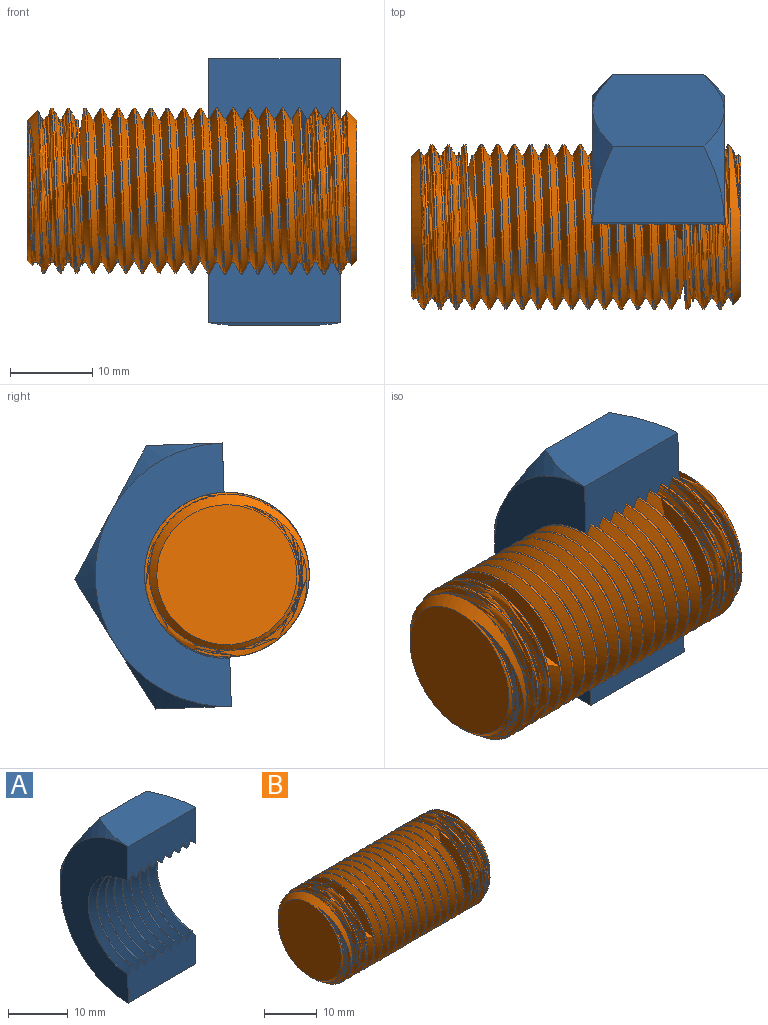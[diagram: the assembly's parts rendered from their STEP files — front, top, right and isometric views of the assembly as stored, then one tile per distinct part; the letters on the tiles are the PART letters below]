
ASSEMBLY  parts=2 mates=1
PART A: 49 faces, bbox 18.7x28.2x37.9 mm
  f0: plane 16x7.23mm, normal (0,-1,0), area 105.3mm2, adj f9,f11,f12,f13,f14,f15,f16,f17
  f1: cone r=18.5mm half-angle=45deg, axis (-1,0,0), area 19.5mm2, adj f2,f4,f47
  f2: plane 16.01x16mm, normal (0,0.87,-0.5), area 264.2mm2, adj f1,f3,f4,f6,f7,f8
  f3: cone r=18.5mm half-angle=45deg, axis (-1,0,0), area 19.5mm2, adj f2,f6,f47
  f4: plane 16.01x16mm, normal (0,0.87,0.5), area 264.2mm2, adj f1,f2,f5,f8,f9,f10
  f5: cone r=18.5mm half-angle=45deg, axis (-1,0,0), area 19.5mm2, adj f4,f9,f47
  f6: plane 16.01x9.24mm, normal (0,0,-1), area 132.1mm2, adj f2,f3,f7,f48
  f7: cone r=18.5mm half-angle=45deg, axis (1,0,0), area 19.5mm2, adj f2,f6,f46
  f8: cone r=18.5mm half-angle=45deg, axis (1,0,0), area 19.5mm2, adj f2,f4,f46
  f9: plane 16.01x9.24mm, normal (0,0,1), area 132.1mm2, adj f0,f4,f5,f10
  f10: cone r=18.5mm half-angle=45deg, axis (1,0,0), area 19.5mm2, adj f4,f9,f46
  f11: cylinder r=8.77mm len=17.53mm, axis (-1,0,0), area 7.2mm2, adj f0,f12,f19,f48
  f12: bspline ~20.54x20.33mm, area 48.1mm2, adj f0,f11,f13,f48
  f13: cylinder r=10.17mm len=20.33mm, axis (-1,0,0), area 3.9mm2, adj f0,f12,f15,f46,f48
  f14: cylinder r=8.77mm len=3.52mm, axis (-1,0,0), area 0.2mm2, adj f0,f15,f46
  f15: bspline ~20.54x20.33mm, area 26.1mm2, adj f0,f13,f14,f46
  f16: cylinder r=8.77mm len=17.53mm, axis (-1,0,0), area 7.2mm2, adj f0,f17,f23,f48
  f17: bspline ~20.54x20.33mm, area 48.1mm2, adj f0,f16,f18,f48
  f18: cylinder r=10.17mm len=20.33mm, axis (-1,0,0), area 4mm2, adj f0,f17,f19,f48
  f19: bspline ~20.54x20.33mm, area 48.1mm2, adj f0,f11,f18,f48
  f20: cylinder r=8.77mm len=17.53mm, axis (-1,0,0), area 7.2mm2, adj f0,f21,f27,f48
  f21: bspline ~20.54x20.33mm, area 48.1mm2, adj f0,f20,f22,f48
  f22: cylinder r=10.17mm len=20.33mm, axis (-1,0,0), area 4mm2, adj f0,f21,f23,f48
  f23: bspline ~20.54x20.33mm, area 48.1mm2, adj f0,f16,f22,f48
  f24: cylinder r=8.77mm len=17.53mm, axis (-1,0,0), area 7.2mm2, adj f0,f25,f31,f48
  f25: bspline ~20.54x20.33mm, area 48.1mm2, adj f0,f24,f26,f48
  f26: cylinder r=10.17mm len=20.33mm, axis (-1,0,0), area 4mm2, adj f0,f25,f27,f48
  f27: bspline ~20.54x20.33mm, area 48.1mm2, adj f0,f20,f26,f48
  f28: cylinder r=8.77mm len=17.53mm, axis (-1,0,0), area 7.2mm2, adj f0,f29,f35,f48
  f29: bspline ~20.54x20.33mm, area 48.1mm2, adj f0,f28,f30,f48
  f30: cylinder r=10.17mm len=20.33mm, axis (-1,0,0), area 4mm2, adj f0,f29,f31,f48
  f31: bspline ~20.54x20.33mm, area 48.1mm2, adj f0,f24,f30,f48
  f32: cylinder r=8.77mm len=17.53mm, axis (-1,0,0), area 7.2mm2, adj f0,f33,f39,f48
  f33: bspline ~20.54x20.33mm, area 48.1mm2, adj f0,f32,f34,f48
  f34: cylinder r=10.17mm len=20.33mm, axis (-1,0,0), area 4mm2, adj f0,f33,f35,f48
  f35: bspline ~20.54x20.33mm, area 48.1mm2, adj f0,f28,f34,f48
  f36: cylinder r=8.77mm len=17.53mm, axis (-1,0,0), area 7.2mm2, adj f0,f37,f43,f48
  f37: bspline ~20.54x20.33mm, area 48.1mm2, adj f0,f36,f38,f48
  f38: cylinder r=10.17mm len=20.33mm, axis (-1,0,0), area 4mm2, adj f0,f37,f39,f48
  f39: bspline ~20.54x20.33mm, area 48.1mm2, adj f0,f32,f38,f48
  f40: cylinder r=8.77mm len=17.53mm, axis (-1,0,0), area 6.9mm2, adj f0,f41,f45,f47,f48
  f41: bspline ~20.54x20.33mm, area 48.1mm2, adj f0,f40,f42,f48
  f42: cylinder r=10.17mm len=20.33mm, axis (-1,0,0), area 4mm2, adj f0,f41,f43,f48
  f43: bspline ~20.54x20.33mm, area 48.1mm2, adj f0,f36,f42,f48
  f44: cylinder r=10.17mm len=2.08mm, axis (-1,0,0), area 0.1mm2, adj f45,f47,f48
  f45: bspline ~20.33x11.74mm, area 22mm2, adj f40,f44,f47,f48
  f46: plane 32.92x16.92mm, normal (-1,0,0), area 262.4mm2, adj f0,f7,f8,f10,f13,f14,f15,f48
  f47: plane 32.92x16.92mm, normal (1,0,0), area 262.4mm2, adj f0,f1,f3,f5,f40,f44,f45,f48
  f48: plane 16x7.23mm, normal (0,-1,0), area 105.3mm2, adj f6,f11,f12,f13,f16,f17,f18,f19
PART B: 8 faces, bbox 41.8x23.1x20 mm
  f0: plane 17x17mm, normal (1,0,0), area 227mm2, adj f3
  f1: cylinder r=10mm len=37mm, axis (-1,0,0), area 568.4mm2, adj f3,f4,f5,f7
  f2: plane 17x17mm, normal (-1,0,0), area 227mm2, adj f4
  f3: cone r=10mm half-angle=45deg, axis (-1,0,0), area 68.4mm2, adj f0,f1,f5,f6,f7
  f4: cone r=8.5mm half-angle=45deg, axis (1,0,0), area 68.4mm2, adj f1,f2,f5,f6,f7
  f5: bspline ~40.75x23.09mm, area 1706.6mm2, adj f1,f3,f4,f6
  f6: cylinder r=8.7mm len=39.6mm, axis (-1,0,0), area 259.2mm2, adj f3,f4,f5,f7
  f7: bspline ~40.75x23.09mm, area 1686.1mm2, adj f1,f3,f4,f6
PLACE A rot(axis=(-1,0,0),2deg) t=(0.57,-3.23,6.79)mm
PLACE B t=(-9.44,-3.23,6.79)mm fixed
MATE cylindrical A.f1 <-> B.f1  axis (1,0,0) through (8.57,-3.23,6.79)mm
